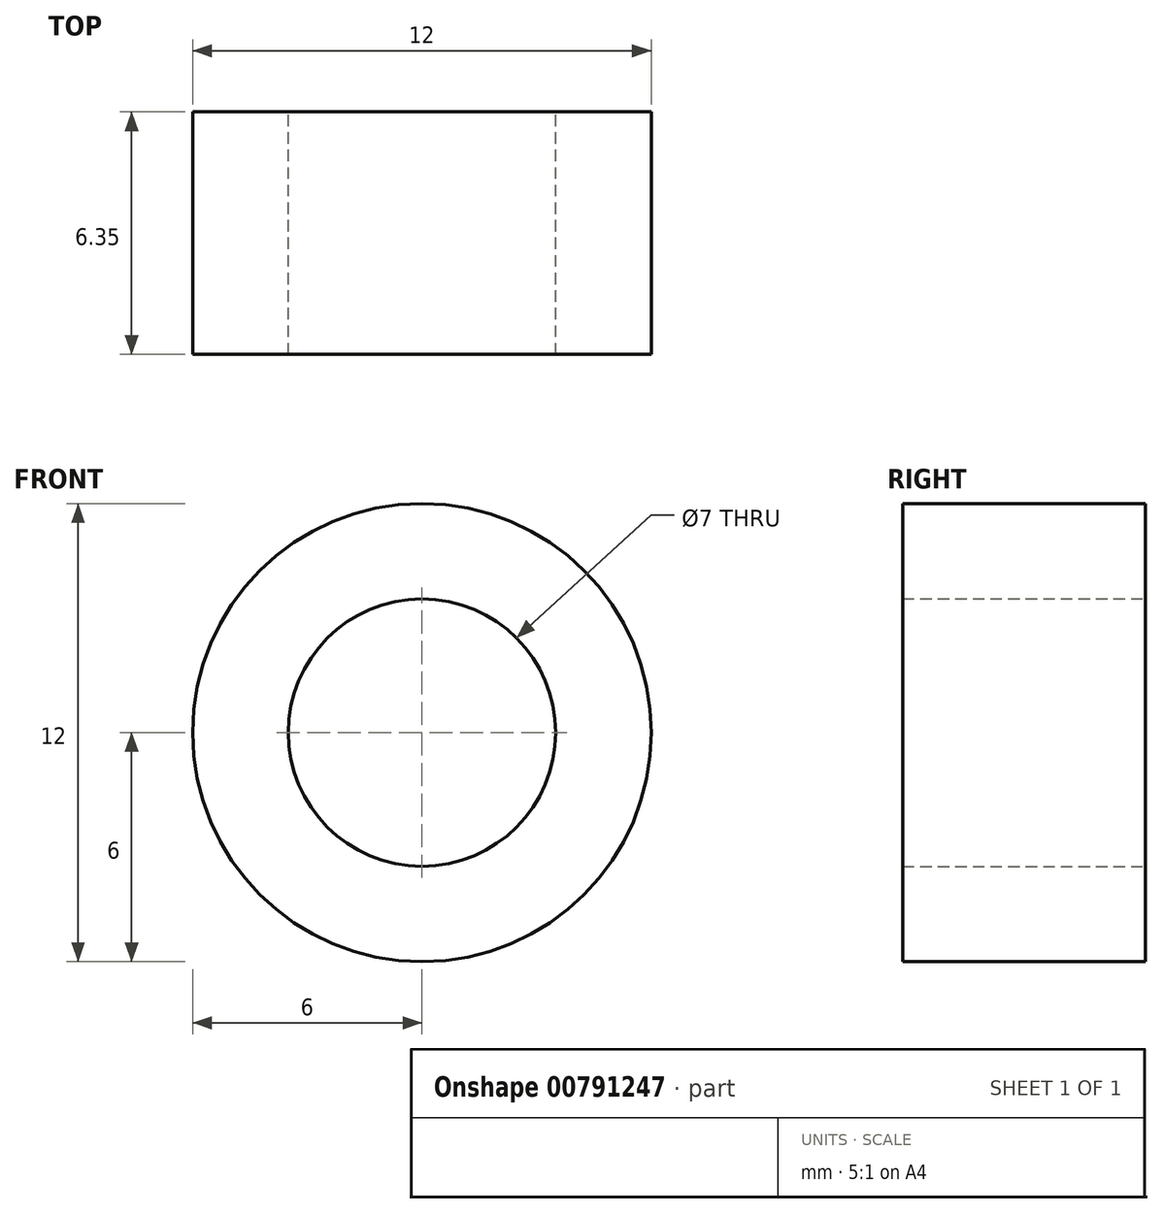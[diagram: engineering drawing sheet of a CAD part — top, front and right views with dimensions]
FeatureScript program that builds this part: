
annotation { "Feature Type Name" : "Feature", "Feature Type Description" : "" }
export const myFeature = defineFeature(function(context is Context, id is Id, definition is map)
    precondition{}
    {
        {
            var Q0;
            Q0=qCreatedBy(makeId("Front.planeOp"),FACE);
            var sketch = newSketch(context, id + "F0", { "sketchPlane" : qUnion([Q0])});
            skCircle(sketch, "E0", {"center": v(0, 0) * mm, "radius": 3.5 * mm});
            skCircle(sketch, "E1", {"center": v(0, 0) * mm, "radius": 6 * mm});
            skSolve(sketch);
        }
        {
            var Q0;
            Q0 = qSketchRegion(id + "F0", true);
            extrude(context, id + "F1", {"entities" : qUnion([Q0]), "depth" : 6.35 * mm, "offsetDistance" : 25 * mm});
        }
    });
